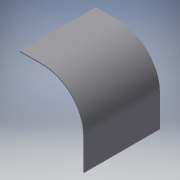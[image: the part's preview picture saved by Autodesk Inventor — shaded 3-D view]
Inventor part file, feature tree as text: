
AUTODESK INVENTOR PART (.ipt)
format: ipt  version: 2019 (Build 230136000, 136)  size: 103,424 bytes
history: native  units: mm
features: thicken_offset x1, sketch x1, other x1, extrude x1
ambient origin geometry x8: Origin, YZ Plane, XZ Plane, XY Plane, X Axis, Y Axis, Z Axis, Center Point
bodies: Solid1 (feature_tree)
feature tree (4):
  thicken_offset  "Thicken1"
  sketch  "Sketch1"  dims[d0=65.0mm d1=50.0mm d2=100.0mm d3=120.0mm d4=0.0mm d5=1.5mm d6=1.0mm]
  other  "Srf1"
  extrude  "ExtrusionSrf1"  Depth=1.5mm
